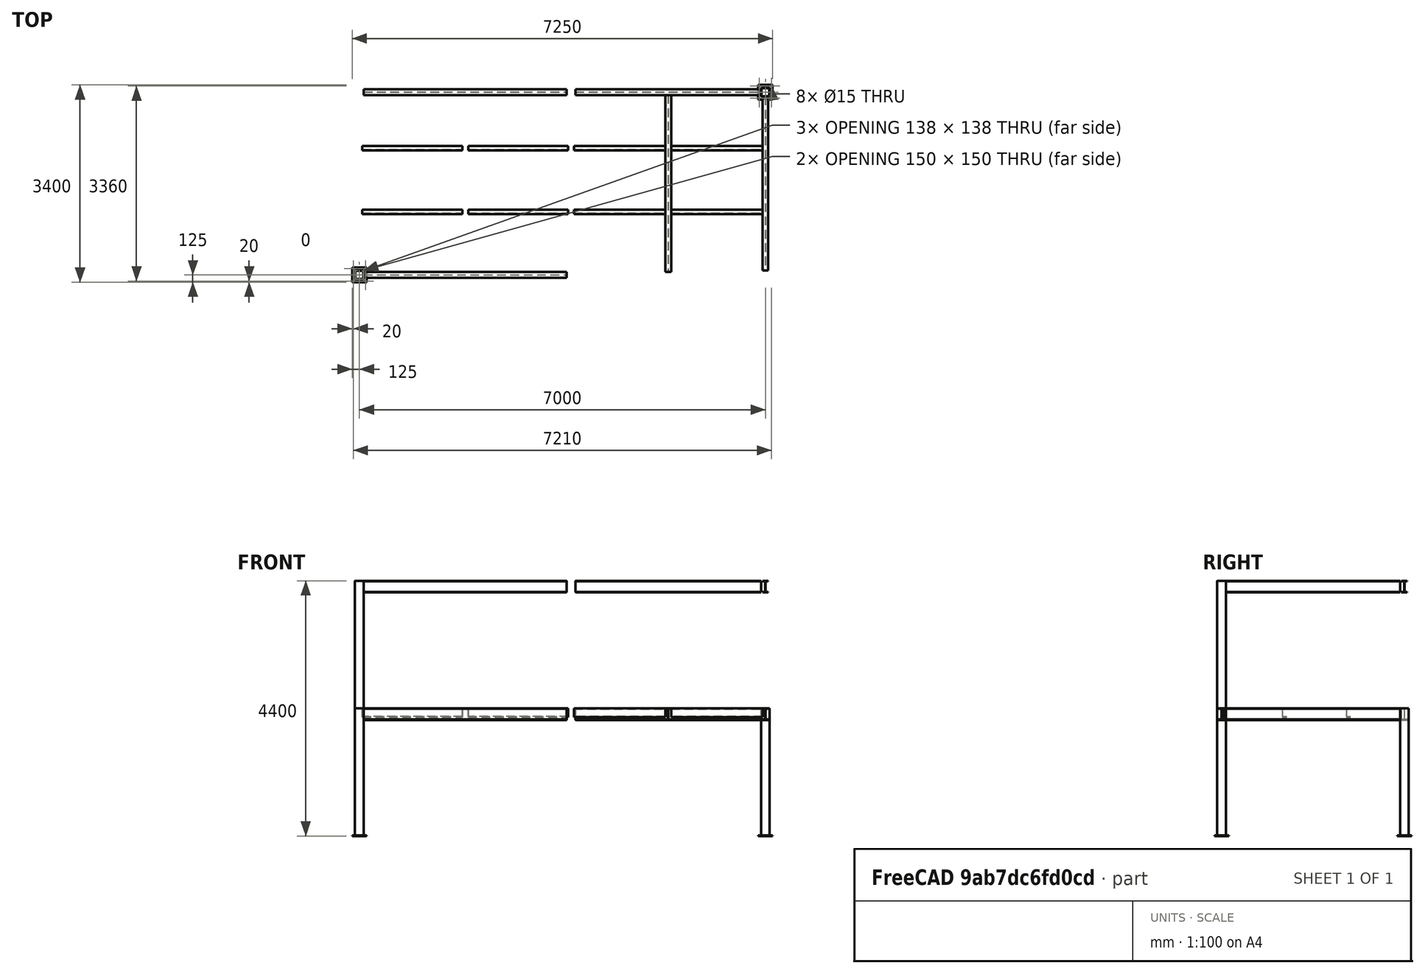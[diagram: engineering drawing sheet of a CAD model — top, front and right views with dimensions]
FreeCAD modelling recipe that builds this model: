
FCSTD DOCUMENT  (FreeCAD 0.21R30492 (Git))
Label: steelframe
License: All rights reserved
LicenseURL: http://en.wikipedia.org/wiki/All_rights_reserved
objects: App::FeaturePython×181, Part::FeaturePython×121, App::Link×12, Part::Extrusion×1, Part::MultiFuse×1
note: 122 computed .brp shape members not serialized (recipe doc carries the construction recipe); baked Part::Feature solids carry a one-line shape summary decoded from their .brp

FEATURE [Part::FeaturePython] BasePlate  # WARN: FeaturePython — macro-defined, semantics opaque (R4)
  B = 250
  D = 15
  H = 250
  b1 = 20
  h1 = 20
  sface = 0
FEATURE [Part::FeaturePython] SquarePipe_SS  # WARN: FeaturePython — macro-defined, semantics opaque (R4)
  L = 2200
  Solid = true
  size = 43
  standard = SS
FEATURE [Part::Extrusion] Extrude
  Base = -> BasePlate
  Dir = (0,0,1)
  DirMode = 2
  FaceMakerClass = Part::FaceMakerBullseye
  LengthFwd = 9
  LengthRev = 0
  Solid = true
  Symmetric = false
FEATURE [Part::MultiFuse] Fusion  label="Square-steel pipe"
  Placement = pos=(1.063e-12,6.983e-12,237) rot=(0,0,1;0rad)
  Shapes = -> [SquarePipe_SS,Extrude]
FEATURE [Part::FeaturePython] H200x100x5_5_8  label="H_thin"  # WARN: FeaturePython — macro-defined, semantics opaque (R4)
  L = 3000
  Placement = pos=(1.2035e-12,3075,2337) rot=(1,0,0;1.5708rad)
  Solid = true
  size = 5
  standard = SS_Thin
FEATURE [App::Link] Link  label="Square-steel pipe001"
  LinkPlacement = pos=(3650,2.14375e-11,237) rot=(0,0,1;0rad)
  LinkedObject = -> Fusion
  Placement = pos=(3650,2.14375e-11,237) rot=(0,0,1;0rad)
FEATURE [Part::FeaturePython] H200x100x5_5_009  label="H_thin001"  # WARN: FeaturePython — macro-defined, semantics opaque (R4)
  L = 3500
  Placement = pos=(75,-3.062e-12,2337) rot=(0.57735,0.57735,0.57735;2.0944rad)
  Solid = true
  size = 5
  standard = SS_Thin
  expr: L = 3500
FEATURE [App::Link] Link001  label="Square-steel pipe002"
  LinkPlacement = pos=(1.0657e-12,3150,237) rot=(0,0,1;0rad)
  LinkedObject = -> Fusion
  Placement = pos=(1.0657e-12,3150,237) rot=(0,0,1;0rad)
FEATURE [Part::FeaturePython] H200x100x5_5_010  label="H_thin002"  # WARN: FeaturePython — macro-defined, semantics opaque (R4)
  L = 3200
  Placement = pos=(3725,-8.67686e-11,2337) rot=(0.57735,0.57735,0.57735;2.0944rad)
  Solid = true
  size = 5
  standard = SS_Thin
FEATURE [App::Link] Link002  label="Square-steel pipe003"
  LinkPlacement = pos=(7000,-1.45687e-10,237) rot=(0,0,1;0rad)
  LinkedObject = -> Link
  Placement = pos=(7000,-1.45687e-10,237) rot=(0,0,1;0rad)
FEATURE [App::Link] Link003  label="H_thin003"
  LinkPlacement = pos=(75,3150,2337) rot=(0.57735,0.57735,0.57735;2.0944rad)
  LinkedObject = -> H200x100x5_5_009
  Placement = pos=(75,3150,2337) rot=(0.57735,0.57735,0.57735;2.0944rad)
FEATURE [App::Link] Link004  label="Square-steel pipe004"
  LinkPlacement = pos=(3650,3150,237) rot=(0,0,1;0rad)
  LinkedObject = -> Link
  Placement = pos=(3650,3150,237) rot=(0,0,1;0rad)
FEATURE [Part::FeaturePython] Clone  label="H_thin004"  # Draft clone (typed FeaturePython)
  AttacherType = Attacher::AttachEngine3D
  Fuse = false
  Objects = -> [H200x100x5_5_8]
  Placement = pos=(3650,3075,2337) rot=(1,0,0;1.5708rad)
  Scale = (1,1,1)
FEATURE [Part::FeaturePython] Clone001  label="H_thin005"  # Draft clone (typed FeaturePython)
  AttacherType = Attacher::AttachEngine3D
  Fuse = false
  Objects = -> [H200x100x5_5_010]
  Placement = pos=(3725,3150,2337) rot=(0.57735,0.57735,0.57735;2.0944rad)
  Scale = (1,1,1)
FEATURE [Part::FeaturePython] Clone002  label="Square-steel pipe005"  # Draft clone (typed FeaturePython)
  AttacherType = Attacher::AttachEngine3D
  Fuse = false
  Objects = -> [Link002]
  Placement = pos=(7000,3150,237) rot=(0,0,1;0rad)
  Scale = (1,1,1)
FEATURE [Part::FeaturePython] Clone003  label="H_thin006"  # Draft clone (typed FeaturePython)
  AttacherType = Attacher::AttachEngine3D
  Fuse = false
  Objects = -> [Clone]
  Placement = pos=(7000,3075,2337) rot=(1,0,0;1.5708rad)
  Scale = (1,1,1)
FEATURE [Part::FeaturePython] H200x100x5_5_011  label="H_thin007"  # WARN: FeaturePython — macro-defined, semantics opaque (R4)
  L = 3050
  Placement = pos=(1825,3100,2337) rot=(1,0,0;1.5708rad)
  Solid = true
  size = 5
  standard = SS_Thin
FEATURE [Part::FeaturePython] Clone004  label="H_thin008"  # Draft clone (typed FeaturePython)
  AttacherType = Attacher::AttachEngine3D
  Fuse = false
  Objects = -> [H200x100x5_5_011]
  Placement = pos=(5325,3100,2337) rot=(1,0,0;1.5708rad)
  Scale = (1,1,1)
FEATURE [Part::FeaturePython] C150x75x007  label="Channel001"  # WARN: FeaturePython — macro-defined, semantics opaque (R4)
  L = 1575
  Placement = pos=(3700,1086.25,2362) rot=(0.57735,0.57735,0.57735;2.0944rad)
  Solid = true
  size = 3
  standard = SS
FEATURE [Part::FeaturePython] C150x75x008  label="Channel002"  # WARN: FeaturePython — macro-defined, semantics opaque (R4)
  L = 1725
  Placement = pos=(50.0219,1086.25,2362) rot=(-0.57735,-0.57735,-0.57735;4.18879rad)
  Solid = true
  size = 3
  standard = SS
FEATURE [Part::FeaturePython] SquarePipe_SS001  label="SQ_Pipe"  # WARN: FeaturePython — macro-defined, semantics opaque (R4)
  L = 2200
  Placement = pos=(1.063e-12,2.583e-12,2437) rot=(0,0,1;2e-06rad)
  Solid = true
  size = 43
  standard = SS
FEATURE [App::Link] Link005  label="SQ_Pipe001"
  LinkPlacement = pos=(1.0843e-12,3150,2437) rot=(0,0,1;0rad)
  LinkedObject = -> SquarePipe_SS001
  Placement = pos=(1.0843e-12,3150,2437) rot=(0,0,1;0rad)
FEATURE [App::Link] Link006  label="SQ_Pipe002"
  LinkPlacement = pos=(3650,-1.01645e-10,2437) rot=(0,0,1;0rad)
  LinkedObject = -> SquarePipe_SS001
  Placement = pos=(3650,-1.01645e-10,2437) rot=(0,0,1;0rad)
FEATURE [App::Link] Link007  label="SQ_Pipe003"
  LinkPlacement = pos=(3650,3150,2437) rot=(0,0,1;0rad)
  LinkedObject = -> Link006
  Placement = pos=(3650,3150,2437) rot=(0,0,1;0rad)
FEATURE [App::Link] Link008  label="SQ_Pipe004"
  LinkPlacement = pos=(7000,6.50122e-10,2437) rot=(0,0,1;0rad)
  LinkedObject = -> Link007
  Placement = pos=(7000,6.50122e-10,2437) rot=(0,0,1;0rad)
FEATURE [App::Link] Link009  label="SQ_Pipe005"
  LinkPlacement = pos=(7000,3150,2437) rot=(0,0,1;0rad)
  LinkedObject = -> Link008
  Placement = pos=(7000,3150,2437) rot=(0,0,1;0rad)
FEATURE [App::Link] Link010  label="H_thin009"
  LinkPlacement = pos=(75,0.000150522,4537) rot=(0.577351,-0.57735,0.57735;4.18879rad)
  LinkedObject = -> H200x100x5_5_009
  Placement = pos=(75,0.000150522,4537) rot=(0.577351,-0.57735,0.57735;4.18879rad)
FEATURE [App::Link] Link011  label="H_thin010"
  LinkPlacement = pos=(-0.000150522,75,4537) rot=(-1,-1e-06,1e-06;1.5708rad)
  LinkedObject = -> H200x100x5_5_8
  Placement = pos=(-0.000150522,75,4537) rot=(-1,-1e-06,1e-06;1.5708rad)
FEATURE [Part::FeaturePython] Clone005  label="H_thin011"  # Draft clone (typed FeaturePython)
  AttacherType = Attacher::AttachEngine3D
  Fuse = false
  Objects = -> [H200x100x5_5_010]
  Placement = pos=(3725,-2.13896e-11,4537) rot=(0.57735,0.57735,0.57735;2.0944rad)
  Scale = (1,1,1)
FEATURE [Part::FeaturePython] Clone006  label="H_thin012"  # Draft clone (typed FeaturePython)
  AttacherType = Attacher::AttachEngine3D
  Fuse = false
  Objects = -> [Link011]
  Placement = pos=(3650,75,4537) rot=(-1,0,0;1.5708rad)
  Scale = (1,1,1)
FEATURE [Part::FeaturePython] Clone007  label="H_thin013"  # Draft clone (typed FeaturePython)
  AttacherType = Attacher::AttachEngine3D
  Fuse = false
  Objects = -> [Clone006]
  Placement = pos=(7000,75,4537) rot=(-1,0,0;1.5708rad)
  Scale = (1,1,1)
FEATURE [Part::FeaturePython] Clone008  label="H_thin014"  # Draft clone (typed FeaturePython)
  AttacherType = Attacher::AttachEngine3D
  Fuse = false
  Objects = -> [Link010]
  Placement = pos=(75,3150,4537) rot=(-0.57735,0.57735,-0.57735;2.0944rad)
  Scale = (1,1,1)
FEATURE [Part::FeaturePython] Clone009  label="H_thin015"  # Draft clone (typed FeaturePython)
  AttacherType = Attacher::AttachEngine3D
  Fuse = false
  Objects = -> [Clone005]
  Placement = pos=(3725,3150,4537) rot=(0.57735,0.57735,0.57735;2.0944rad)
  Scale = (1,1,1)
FEATURE [Part::FeaturePython] Array002  # Draft array (typed FeaturePython)
  Angle = 360
  ArrayType = 0
  Axis = (0,0,1)
  Base = -> C150x75x007
  Center = (0,0,0)
  Fuse = false
  IntervalAxis = (0,0,0)
  IntervalX = (1675,0,0)
  IntervalY = (0,1100,0)
  IntervalZ = (0,0,50)
  NumberCircles = 3
  NumberPolar = 5
  NumberX = 2
  NumberY = 2
  NumberZ = 1
  RadialDistance = 50
  Symmetry = 1
  TangentialDistance = 25
FEATURE [Part::FeaturePython] Array  # Draft array (typed FeaturePython)
  Angle = 360
  ArrayType = 0
  Axis = (0,0,1)
  Base = -> C150x75x008
  Center = (0,0,0)
  Fuse = false
  IntervalAxis = (0,0,0)
  IntervalX = (1826,0,0)
  IntervalY = (0,1100,0)
  IntervalZ = (0,0,50)
  NumberCircles = 3
  NumberPolar = 5
  NumberX = 2
  NumberY = 2
  NumberZ = 1
  RadialDistance = 50
  Symmetry = 1
  TangentialDistance = 25
FEATURE [Part::FeaturePython] Parts  # WARN: FeaturePython — macro-defined, semantics opaque (R4)
  Group = -> [Fusion,H200x100x5_5_8,Link,H200x100x5_5_009,Link001,H200x100x5_5_010,Link002,Link003,Link004,Clone,Clone001,Clone002,Clone003,H200x100x5_5_011,Clone004,C150x75x007,C150x75x008,SquarePipe_SS001,Link005,Link006,Link007,Link008,Link009,Link010,Link011,Clone005,Clone006,Clone007,Clone008,Clone009,Array002,Array]
  GroupMode = 0
FEATURE [Part::FeaturePython] Assembly  # WARN: FeaturePython — macro-defined, semantics opaque (R4)
  AutoRelax = true
  BuildShape = 0
  Freeze = false
  Group = -> [Constraints,Elements,Parts]
  Verbose = false
  _SolverType = 1
  _Version = 1
FEATURE [App::FeaturePython] Constraints  # WARN: FeaturePython — macro-defined, semantics opaque (R4)
  Group = -> [Constraint,Constraint001,Constraint002,Constraint003,Constraint004,Constraint005,Constraint006,Constraint007,Constraint008,Constraint009,Constraint010,Constraint011,Constraint012,Constraint013,Constraint014,Constraint015,Constraint016,Constraint017,Constraint018,Constraint019,Constraint020,Constraint021,Constraint022,Constraint023,Constraint024,Constraint025,Constraint026,Constraint027,+32 more]
  _Version = 1
FEATURE [App::FeaturePython] Elements  # WARN: FeaturePython — macro-defined, semantics opaque (R4)
  Group = -> [_Element,_Element001,_Element002,_Element003,_Element004,_Element005,_Element006,_Element007,_Element008,_Element009,_Element010,_Element011,_Element012,_Element013,_Element014,_Element015,_Element016,_Element017,_Element018,_Element019,_Element020,_Element021,_Element022,_Element023,_Element024,_Element025,_Element026,_Element027,_Element028,_Element029,_Element030,_Element031,_Element032,+65 more]
FEATURE [App::FeaturePython] Constraint  label="PlaneCoincident"  # WARN: FeaturePython — macro-defined, semantics opaque (R4)
  Angle = 0
  AnglePitch = 0
  AngleRoll = 0
  Cascade = false
  Disabled = false
  Group = -> [ElementLink,ElementLink001]
  LockAngle = false
  Multiply = false
  OffsetX = 0
  OffsetY = 0
  _ConstraintType = 35
  _Parent = -> Constraints
FEATURE [App::FeaturePython] ElementLink  label="_Element"  # link proxy (typed FeaturePython)
  LinkTransform = true
  LinkedObject = -> _Element
  _Parent = -> Constraint
FEATURE [Part::FeaturePython] _Element  # link proxy (typed FeaturePython)
  Detach = false
  LinkTransform = true
  LinkedObject = -> SquarePipe_SS001 [Face17]
  _Parent = -> Elements
FEATURE [App::FeaturePython] ElementLink001  label="_Element001"  # link proxy (typed FeaturePython)
  LinkTransform = true
  LinkedObject = -> _Element001
  _Parent = -> Constraint
FEATURE [Part::FeaturePython] _Element001  # link proxy (typed FeaturePython)
  Detach = false
  LinkTransform = true
  LinkedObject = -> Fusion [Face21]
  _Parent = -> Elements
FEATURE [Part::FeaturePython] _Element002  # link proxy (typed FeaturePython)
  Detach = false
  LinkTransform = true
  LinkedObject = -> H200x100x5_5_009 [Edge47]
  _Parent = -> Elements
FEATURE [Part::FeaturePython] _Element003  # link proxy (typed FeaturePython)
  Detach = false
  LinkTransform = true
  LinkedObject = -> Fusion [Edge59]
  _Parent = -> Elements
FEATURE [App::FeaturePython] Constraint001  label="Locked"  # WARN: FeaturePython — macro-defined, semantics opaque (R4)
  Disabled = false
  Group = -> [ElementLink002]
  _ConstraintType = 0
  _Parent = -> Constraints
FEATURE [App::FeaturePython] ElementLink002  label="_Element004"  # link proxy (typed FeaturePython)
  LinkTransform = true
  LinkedObject = -> _Element004
  _Parent = -> Constraint001
FEATURE [Part::FeaturePython] _Element004  # link proxy (typed FeaturePython)
  Detach = false
  LinkTransform = true
  LinkedObject = -> Fusion [Face16]
  _Parent = -> Elements
FEATURE [App::FeaturePython] Constraint002  label="MidPoint"  # WARN: FeaturePython — macro-defined, semantics opaque (R4)
  Disabled = false
  Group = -> [ElementLink003,ElementLink004]
  _ConstraintType = 20
  _Parent = -> Constraints
FEATURE [App::FeaturePython] ElementLink003  label="_Element002"  # link proxy (typed FeaturePython)
  LinkTransform = true
  LinkedObject = -> _Element002
  _Parent = -> Constraint002
FEATURE [App::FeaturePython] ElementLink004  label="_Element003"  # link proxy (typed FeaturePython)
  LinkTransform = true
  LinkedObject = -> _Element003
  _Parent = -> Constraint002
FEATURE [Part::FeaturePython] _Element005  # link proxy (typed FeaturePython)
  Detach = false
  LinkTransform = true
  LinkedObject = -> H200x100x5_5_009 [Vertex15]
  _Parent = -> Elements
FEATURE [App::FeaturePython] Constraint003  label="PlaneAlignment"  # WARN: FeaturePython — macro-defined, semantics opaque (R4)
  Angle = 0
  AnglePitch = 0
  AngleRoll = 0
  Cascade = false
  Disabled = false
  Group = -> [ElementLink005,ElementLink006]
  LockAngle = false
  _ConstraintType = 37
  _Parent = -> Constraints
FEATURE [App::FeaturePython] ElementLink005  label="_Element006"  # link proxy (typed FeaturePython)
  LinkTransform = true
  LinkedObject = -> _Element006
  _Parent = -> Constraint003
FEATURE [Part::FeaturePython] _Element006  # link proxy (typed FeaturePython)
  Detach = false
  LinkTransform = true
  LinkedObject = -> H200x100x5_5_009 [Face16]
  _Parent = -> Elements
FEATURE [App::FeaturePython] ElementLink006  label="_Element001"  # link proxy (typed FeaturePython)
  LinkTransform = true
  LinkedObject = -> _Element001
  _Parent = -> Constraint003
FEATURE [App::FeaturePython] Constraint004  label="SameOrientation"  # WARN: FeaturePython — macro-defined, semantics opaque (R4)
  Disabled = false
  Group = -> [ElementLink007,ElementLink008]
  _ConstraintType = 2
  _Parent = -> Constraints
FEATURE [App::FeaturePython] ElementLink007  label="_Element006"  # link proxy (typed FeaturePython)
  LinkTransform = true
  LinkedObject = -> _Element006
  _Parent = -> Constraint004
FEATURE [App::FeaturePython] ElementLink008  label="_Element001"  # link proxy (typed FeaturePython)
  LinkTransform = true
  LinkedObject = -> _Element001
  _Parent = -> Constraint004
FEATURE [App::FeaturePython] Constraint005  label="MidPoint001"  # WARN: FeaturePython — macro-defined, semantics opaque (R4)
  Disabled = false
  Group = -> [ElementLink009,ElementLink010]
  _ConstraintType = 20
  _Parent = -> Constraints
FEATURE [App::FeaturePython] ElementLink009  label="_Element007"  # link proxy (typed FeaturePython)
  LinkTransform = true
  LinkedObject = -> _Element007
  _Parent = -> Constraint005
FEATURE [Part::FeaturePython] _Element007  # link proxy (typed FeaturePython)
  Detach = false
  LinkTransform = true
  LinkedObject = -> H200x100x5_5_009 [Edge48]
  _Parent = -> Elements
FEATURE [App::FeaturePython] ElementLink010  label="_Element008"  # link proxy (typed FeaturePython)
  LinkTransform = true
  LinkedObject = -> _Element008
  _Parent = -> Constraint005
FEATURE [Part::FeaturePython] _Element008  # link proxy (typed FeaturePython)
  Detach = false
  LinkTransform = true
  LinkedObject = -> Link [Edge50]
  _Parent = -> Elements
FEATURE [App::FeaturePython] Constraint006  label="SameOrientation001"  # WARN: FeaturePython — macro-defined, semantics opaque (R4)
  Disabled = false
  Group = -> [ElementLink011,ElementLink012]
  _ConstraintType = 2
  _Parent = -> Constraints
FEATURE [App::FeaturePython] ElementLink011  label="_Element006"  # link proxy (typed FeaturePython)
  LinkTransform = true
  LinkedObject = -> _Element006
  _Parent = -> Constraint006
FEATURE [App::FeaturePython] ElementLink012  label="_Element009"  # link proxy (typed FeaturePython)
  LinkTransform = true
  LinkedObject = -> _Element009
  _Parent = -> Constraint006
FEATURE [Part::FeaturePython] _Element009  # link proxy (typed FeaturePython)
  Detach = false
  LinkTransform = true
  LinkedObject = -> Link [Face21]
  _Parent = -> Elements
FEATURE [App::FeaturePython] Constraint007  label="MidPoint002"  # WARN: FeaturePython — macro-defined, semantics opaque (R4)
  Disabled = false
  Group = -> [ElementLink013,ElementLink014]
  _ConstraintType = 20
  _Parent = -> Constraints
FEATURE [App::FeaturePython] ElementLink013  label="_Element010"  # link proxy (typed FeaturePython)
  LinkTransform = true
  LinkedObject = -> _Element010
  _Parent = -> Constraint007
FEATURE [Part::FeaturePython] _Element010  # link proxy (typed FeaturePython)
  Detach = false
  LinkTransform = true
  LinkedObject = -> Link006 [Edge18]
  _Parent = -> Elements
FEATURE [App::FeaturePython] ElementLink014  label="_Element011"  # link proxy (typed FeaturePython)
  LinkTransform = true
  LinkedObject = -> _Element011
  _Parent = -> Constraint007
FEATURE [Part::FeaturePython] _Element011  # link proxy (typed FeaturePython)
  Detach = false
  LinkTransform = true
  LinkedObject = -> Link [Edge55]
  _Parent = -> Elements
FEATURE [App::FeaturePython] Constraint008  label="SameOrientation002"  # WARN: FeaturePython — macro-defined, semantics opaque (R4)
  Disabled = false
  Group = -> [ElementLink015,ElementLink016]
  _ConstraintType = 2
  _Parent = -> Constraints
FEATURE [App::FeaturePython] ElementLink015  label="_Element012"  # link proxy (typed FeaturePython)
  LinkTransform = true
  LinkedObject = -> _Element012
  _Parent = -> Constraint008
FEATURE [Part::FeaturePython] _Element012  # link proxy (typed FeaturePython)
  Detach = false
  LinkTransform = true
  LinkedObject = -> Link006 [Face6]
  _Parent = -> Elements
FEATURE [App::FeaturePython] ElementLink016  label="_Element013"  # link proxy (typed FeaturePython)
  LinkTransform = true
  LinkedObject = -> _Element013
  _Parent = -> Constraint008
FEATURE [Part::FeaturePython] _Element013  # link proxy (typed FeaturePython)
  Detach = false
  LinkTransform = true
  LinkedObject = -> Link [Face14]
  _Parent = -> Elements
FEATURE [App::FeaturePython] Constraint009  label="MidPoint003"  # WARN: FeaturePython — macro-defined, semantics opaque (R4)
  Disabled = false
  Group = -> [ElementLink017,ElementLink018]
  _ConstraintType = 20
  _Parent = -> Constraints
FEATURE [App::FeaturePython] ElementLink017  label="_Element014"  # link proxy (typed FeaturePython)
  LinkTransform = true
  LinkedObject = -> _Element014
  _Parent = -> Constraint009
FEATURE [Part::FeaturePython] _Element014  # link proxy (typed FeaturePython)
  Detach = false
  LinkTransform = true
  LinkedObject = -> H200x100x5_5_010 [Edge47]
  _Parent = -> Elements
FEATURE [App::FeaturePython] ElementLink018  label="_Element015"  # link proxy (typed FeaturePython)
  LinkTransform = true
  LinkedObject = -> _Element015
  _Parent = -> Constraint009
FEATURE [Part::FeaturePython] _Element015  # link proxy (typed FeaturePython)
  Detach = false
  LinkTransform = true
  LinkedObject = -> Link006 [Edge12]
  _Parent = -> Elements
FEATURE [App::FeaturePython] Constraint010  label="SameOrientation003"  # WARN: FeaturePython — macro-defined, semantics opaque (R4)
  Disabled = false
  Group = -> [ElementLink019,ElementLink020]
  _ConstraintType = 2
  _Parent = -> Constraints
FEATURE [App::FeaturePython] ElementLink019  label="_Element016"  # link proxy (typed FeaturePython)
  LinkTransform = true
  LinkedObject = -> _Element016
  _Parent = -> Constraint010
FEATURE [Part::FeaturePython] _Element016  # link proxy (typed FeaturePython)
  Detach = false
  LinkTransform = true
  LinkedObject = -> H200x100x5_5_010 [Face16]
  _Parent = -> Elements
FEATURE [App::FeaturePython] ElementLink020  label="_Element009"  # link proxy (typed FeaturePython)
  LinkTransform = true
  LinkedObject = -> _Element009
  _Parent = -> Constraint010
FEATURE [App::FeaturePython] Constraint011  label="MidPoint004"  # WARN: FeaturePython — macro-defined, semantics opaque (R4)
  Disabled = false
  Group = -> [ElementLink021,ElementLink022]
  _ConstraintType = 20
  _Parent = -> Constraints
FEATURE [App::FeaturePython] ElementLink021  label="_Element017"  # link proxy (typed FeaturePython)
  LinkTransform = true
  LinkedObject = -> _Element017
  _Parent = -> Constraint011
FEATURE [Part::FeaturePython] _Element017  # link proxy (typed FeaturePython)
  Detach = false
  LinkTransform = true
  LinkedObject = -> Link002 [Edge50]
  _Parent = -> Elements
FEATURE [App::FeaturePython] ElementLink022  label="_Element018"  # link proxy (typed FeaturePython)
  LinkTransform = true
  LinkedObject = -> _Element018
  _Parent = -> Constraint011
FEATURE [Part::FeaturePython] _Element018  # link proxy (typed FeaturePython)
  Detach = false
  LinkTransform = true
  LinkedObject = -> H200x100x5_5_010 [Edge48]
  _Parent = -> Elements
FEATURE [App::FeaturePython] Constraint012  label="SameOrientation004"  # WARN: FeaturePython — macro-defined, semantics opaque (R4)
  Disabled = false
  Group = -> [ElementLink023,ElementLink024]
  _ConstraintType = 2
  _Parent = -> Constraints
FEATURE [App::FeaturePython] ElementLink023  label="_Element016"  # link proxy (typed FeaturePython)
  LinkTransform = true
  LinkedObject = -> _Element016
  _Parent = -> Constraint012
FEATURE [App::FeaturePython] ElementLink024  label="_Element019"  # link proxy (typed FeaturePython)
  LinkTransform = true
  LinkedObject = -> _Element019
  _Parent = -> Constraint012
FEATURE [Part::FeaturePython] _Element019  # link proxy (typed FeaturePython)
  Detach = false
  LinkTransform = true
  LinkedObject = -> Link002 [Face21]
  _Parent = -> Elements
FEATURE [App::FeaturePython] Constraint013  label="MidPoint005"  # WARN: FeaturePython — macro-defined, semantics opaque (R4)
  Disabled = false
  Group = -> [ElementLink025,ElementLink026]
  _ConstraintType = 20
  _Parent = -> Constraints
FEATURE [App::FeaturePython] ElementLink025  label="_Element020"  # link proxy (typed FeaturePython)
  LinkTransform = true
  LinkedObject = -> _Element020
  _Parent = -> Constraint013
FEATURE [Part::FeaturePython] _Element020  # link proxy (typed FeaturePython)
  Detach = false
  LinkTransform = true
  LinkedObject = -> Link008 [Edge18]
  _Parent = -> Elements
FEATURE [App::FeaturePython] ElementLink026  label="_Element021"  # link proxy (typed FeaturePython)
  LinkTransform = true
  LinkedObject = -> _Element021
  _Parent = -> Constraint013
FEATURE [Part::FeaturePython] _Element021  # link proxy (typed FeaturePython)
  Detach = false
  LinkTransform = true
  LinkedObject = -> Link002 [Edge55]
  _Parent = -> Elements
FEATURE [App::FeaturePython] Constraint014  label="SameOrientation005"  # WARN: FeaturePython — macro-defined, semantics opaque (R4)
  Disabled = false
  Group = -> [ElementLink027,ElementLink028]
  _ConstraintType = 2
  _Parent = -> Constraints
FEATURE [App::FeaturePython] ElementLink027  label="_Element022"  # link proxy (typed FeaturePython)
  LinkTransform = true
  LinkedObject = -> _Element022
  _Parent = -> Constraint014
FEATURE [Part::FeaturePython] _Element022  # link proxy (typed FeaturePython)
  Detach = false
  LinkTransform = true
  LinkedObject = -> Link008 [Face6]
  _Parent = -> Elements
FEATURE [App::FeaturePython] ElementLink028  label="_Element023"  # link proxy (typed FeaturePython)
  LinkTransform = true
  LinkedObject = -> _Element023
  _Parent = -> Constraint014
FEATURE [Part::FeaturePython] _Element023  # link proxy (typed FeaturePython)
  Detach = false
  LinkTransform = true
  LinkedObject = -> Link002 [Face14]
  _Parent = -> Elements
FEATURE [App::FeaturePython] Constraint015  label="MidPoint006"  # WARN: FeaturePython — macro-defined, semantics opaque (R4)
  Disabled = false
  Group = -> [ElementLink029,ElementLink030]
  _ConstraintType = 20
  _Parent = -> Constraints
FEATURE [App::FeaturePython] ElementLink029  label="_Element024"  # link proxy (typed FeaturePython)
  LinkTransform = true
  LinkedObject = -> _Element024
  _Parent = -> Constraint015
FEATURE [Part::FeaturePython] _Element024  # link proxy (typed FeaturePython)
  Detach = false
  LinkTransform = true
  LinkedObject = -> H200x100x5_5_8 [Edge48]
  _Parent = -> Elements
FEATURE [App::FeaturePython] ElementLink030  label="_Element025"  # link proxy (typed FeaturePython)
  LinkTransform = true
  LinkedObject = -> _Element025
  _Parent = -> Constraint015
FEATURE [Part::FeaturePython] _Element025  # link proxy (typed FeaturePython)
  Detach = false
  LinkTransform = true
  LinkedObject = -> Fusion [Edge63]
  _Parent = -> Elements
FEATURE [App::FeaturePython] Constraint016  label="SameOrientation006"  # WARN: FeaturePython — macro-defined, semantics opaque (R4)
  Disabled = false
  Group = -> [ElementLink031,ElementLink032]
  _ConstraintType = 2
  _Parent = -> Constraints
FEATURE [App::FeaturePython] ElementLink031  label="_Element026"  # link proxy (typed FeaturePython)
  LinkTransform = true
  LinkedObject = -> _Element026
  _Parent = -> Constraint016
FEATURE [Part::FeaturePython] _Element026  # link proxy (typed FeaturePython)
  Detach = false
  LinkTransform = true
  LinkedObject = -> H200x100x5_5_8 [Face16]
  _Parent = -> Elements
FEATURE [App::FeaturePython] ElementLink032  label="_Element001"  # link proxy (typed FeaturePython)
  LinkTransform = true
  LinkedObject = -> _Element001
  _Parent = -> Constraint016
FEATURE [App::FeaturePython] Constraint017  label="MidPoint007"  # WARN: FeaturePython — macro-defined, semantics opaque (R4)
  Disabled = false
  Group = -> [ElementLink033,ElementLink034]
  _ConstraintType = 20
  _Parent = -> Constraints
FEATURE [App::FeaturePython] ElementLink033  label="_Element027"  # link proxy (typed FeaturePython)
  LinkTransform = true
  LinkedObject = -> _Element027
  _Parent = -> Constraint017
FEATURE [Part::FeaturePython] _Element027  # link proxy (typed FeaturePython)
  Detach = false
  LinkTransform = true
  LinkedObject = -> Clone [Edge48]
  _Parent = -> Elements
FEATURE [App::FeaturePython] ElementLink034  label="_Element028"  # link proxy (typed FeaturePython)
  LinkTransform = true
  LinkedObject = -> _Element028
  _Parent = -> Constraint017
FEATURE [Part::FeaturePython] _Element028  # link proxy (typed FeaturePython)
  Detach = false
  LinkTransform = true
  LinkedObject = -> Link [Edge63]
  _Parent = -> Elements
FEATURE [App::FeaturePython] Constraint018  label="SameOrientation007"  # WARN: FeaturePython — macro-defined, semantics opaque (R4)
  Disabled = false
  Group = -> [ElementLink035,ElementLink036]
  _ConstraintType = 2
  _Parent = -> Constraints
FEATURE [App::FeaturePython] ElementLink035  label="_Element029"  # link proxy (typed FeaturePython)
  LinkTransform = true
  LinkedObject = -> _Element029
  _Parent = -> Constraint018
FEATURE [Part::FeaturePython] _Element029  # link proxy (typed FeaturePython)
  Detach = false
  LinkTransform = true
  LinkedObject = -> Clone [Face16]
  _Parent = -> Elements
FEATURE [App::FeaturePython] ElementLink036  label="_Element009"  # link proxy (typed FeaturePython)
  LinkTransform = true
  LinkedObject = -> _Element009
  _Parent = -> Constraint018
FEATURE [App::FeaturePython] Constraint019  label="MidPoint008"  # WARN: FeaturePython — macro-defined, semantics opaque (R4)
  Disabled = false
  Group = -> [ElementLink037,ElementLink038]
  _ConstraintType = 20
  _Parent = -> Constraints
FEATURE [App::FeaturePython] ElementLink037  label="_Element030"  # link proxy (typed FeaturePython)
  LinkTransform = true
  LinkedObject = -> _Element030
  _Parent = -> Constraint019
FEATURE [Part::FeaturePython] _Element030  # link proxy (typed FeaturePython)
  Detach = false
  LinkTransform = true
  LinkedObject = -> Clone003 [Edge48]
  _Parent = -> Elements
FEATURE [App::FeaturePython] ElementLink038  label="_Element031"  # link proxy (typed FeaturePython)
  LinkTransform = true
  LinkedObject = -> _Element031
  _Parent = -> Constraint019
FEATURE [Part::FeaturePython] _Element031  # link proxy (typed FeaturePython)
  Detach = false
  LinkTransform = true
  LinkedObject = -> Link002 [Edge63]
  _Parent = -> Elements
FEATURE [App::FeaturePython] Constraint020  label="SameOrientation008"  # WARN: FeaturePython — macro-defined, semantics opaque (R4)
  Disabled = false
  Group = -> [ElementLink039,ElementLink040]
  _ConstraintType = 2
  _Parent = -> Constraints
FEATURE [App::FeaturePython] ElementLink039  label="_Element032"  # link proxy (typed FeaturePython)
  LinkTransform = true
  LinkedObject = -> _Element032
  _Parent = -> Constraint020
FEATURE [Part::FeaturePython] _Element032  # link proxy (typed FeaturePython)
  Detach = false
  LinkTransform = true
  LinkedObject = -> Clone003 [Face16]
  _Parent = -> Elements
FEATURE [App::FeaturePython] ElementLink040  label="_Element019"  # link proxy (typed FeaturePython)
  LinkTransform = true
  LinkedObject = -> _Element019
  _Parent = -> Constraint020
FEATURE [App::FeaturePython] Constraint021  label="MidPoint009"  # WARN: FeaturePython — macro-defined, semantics opaque (R4)
  Disabled = false
  Group = -> [ElementLink041,ElementLink042]
  _ConstraintType = 20
  _Parent = -> Constraints
FEATURE [App::FeaturePython] ElementLink041  label="_Element033"  # link proxy (typed FeaturePython)
  LinkTransform = true
  LinkedObject = -> _Element033
  _Parent = -> Constraint021
FEATURE [Part::FeaturePython] _Element033  # link proxy (typed FeaturePython)
  Detach = false
  LinkTransform = true
  LinkedObject = -> Link001 [Edge55]
  _Parent = -> Elements
FEATURE [App::FeaturePython] ElementLink042  label="_Element034"  # link proxy (typed FeaturePython)
  LinkTransform = true
  LinkedObject = -> _Element034
  _Parent = -> Constraint021
FEATURE [Part::FeaturePython] _Element034  # link proxy (typed FeaturePython)
  Detach = false
  LinkTransform = true
  LinkedObject = -> H200x100x5_5_8 [Edge47]
  _Parent = -> Elements
FEATURE [App::FeaturePython] Constraint022  label="SameOrientation009"  # WARN: FeaturePython — macro-defined, semantics opaque (R4)
  Disabled = false
  Group = -> [ElementLink043,ElementLink044]
  _ConstraintType = 2
  _Parent = -> Constraints
FEATURE [App::FeaturePython] ElementLink043  label="_Element026"  # link proxy (typed FeaturePython)
  LinkTransform = true
  LinkedObject = -> _Element026
  _Parent = -> Constraint022
FEATURE [App::FeaturePython] ElementLink044  label="_Element035"  # link proxy (typed FeaturePython)
  LinkTransform = true
  LinkedObject = -> _Element035
  _Parent = -> Constraint022
FEATURE [Part::FeaturePython] _Element035  # link proxy (typed FeaturePython)
  Detach = false
  LinkTransform = true
  LinkedObject = -> Link001 [Face21]
  _Parent = -> Elements
FEATURE [App::FeaturePython] Constraint023  label="MidPoint010"  # WARN: FeaturePython — macro-defined, semantics opaque (R4)
  Disabled = false
  Group = -> [ElementLink045,ElementLink046]
  _ConstraintType = 20
  _Parent = -> Constraints
FEATURE [App::FeaturePython] ElementLink045  label="_Element036"  # link proxy (typed FeaturePython)
  LinkTransform = true
  LinkedObject = -> _Element036
  _Parent = -> Constraint023
FEATURE [Part::FeaturePython] _Element036  # link proxy (typed FeaturePython)
  Detach = false
  LinkTransform = true
  LinkedObject = -> Link005 [Edge12]
  _Parent = -> Elements
FEATURE [App::FeaturePython] ElementLink046  label="_Element037"  # link proxy (typed FeaturePython)
  LinkTransform = true
  LinkedObject = -> _Element037
  _Parent = -> Constraint023
FEATURE [Part::FeaturePython] _Element037  # link proxy (typed FeaturePython)
  Detach = false
  LinkTransform = true
  LinkedObject = -> Link001 [Edge59]
  _Parent = -> Elements
FEATURE [App::FeaturePython] Constraint024  label="SameOrientation010"  # WARN: FeaturePython — macro-defined, semantics opaque (R4)
  Disabled = false
  Group = -> [ElementLink047,ElementLink048]
  _ConstraintType = 2
  _Parent = -> Constraints
FEATURE [App::FeaturePython] ElementLink047  label="_Element038"  # link proxy (typed FeaturePython)
  LinkTransform = true
  LinkedObject = -> _Element038
  _Parent = -> Constraint024
FEATURE [Part::FeaturePython] _Element038  # link proxy (typed FeaturePython)
  Detach = false
  LinkTransform = true
  LinkedObject = -> Link001 [Face16]
  _Parent = -> Elements
FEATURE [App::FeaturePython] ElementLink048  label="_Element039"  # link proxy (typed FeaturePython)
  LinkTransform = true
  LinkedObject = -> _Element039
  _Parent = -> Constraint024
FEATURE [Part::FeaturePython] _Element039  # link proxy (typed FeaturePython)
  Detach = false
  LinkTransform = true
  LinkedObject = -> Link005 [Face4]
  _Parent = -> Elements
FEATURE [App::FeaturePython] Constraint025  label="MidPoint011"  # WARN: FeaturePython — macro-defined, semantics opaque (R4)
  Disabled = false
  Group = -> [ElementLink049,ElementLink050]
  _ConstraintType = 20
  _Parent = -> Constraints
FEATURE [App::FeaturePython] ElementLink049  label="_Element040"  # link proxy (typed FeaturePython)
  LinkTransform = true
  LinkedObject = -> _Element040
  _Parent = -> Constraint025
FEATURE [Part::FeaturePython] _Element040  # link proxy (typed FeaturePython)
  Detach = false
  LinkTransform = true
  LinkedObject = -> Clone [Edge47]
  _Parent = -> Elements
FEATURE [App::FeaturePython] ElementLink050  label="_Element041"  # link proxy (typed FeaturePython)
  LinkTransform = true
  LinkedObject = -> _Element041
  _Parent = -> Constraint025
FEATURE [Part::FeaturePython] _Element041  # link proxy (typed FeaturePython)
  Detach = false
  LinkTransform = true
  LinkedObject = -> Link004 [Edge55]
  _Parent = -> Elements
FEATURE [App::FeaturePython] Constraint026  label="SameOrientation011"  # WARN: FeaturePython — macro-defined, semantics opaque (R4)
  Disabled = false
  Group = -> [ElementLink051,ElementLink052]
  _ConstraintType = 2
  _Parent = -> Constraints
FEATURE [App::FeaturePython] ElementLink051  label="_Element029"  # link proxy (typed FeaturePython)
  LinkTransform = true
  LinkedObject = -> _Element029
  _Parent = -> Constraint026
FEATURE [App::FeaturePython] ElementLink052  label="_Element042"  # link proxy (typed FeaturePython)
  LinkTransform = true
  LinkedObject = -> _Element042
  _Parent = -> Constraint026
FEATURE [Part::FeaturePython] _Element042  # link proxy (typed FeaturePython)
  Detach = false
  LinkTransform = true
  LinkedObject = -> Link004 [Face21]
  _Parent = -> Elements
FEATURE [App::FeaturePython] Constraint027  label="MidPoint012"  # WARN: FeaturePython — macro-defined, semantics opaque (R4)
  Disabled = false
  Group = -> [ElementLink053,ElementLink054]
  _ConstraintType = 20
  _Parent = -> Constraints
FEATURE [App::FeaturePython] ElementLink053  label="_Element043"  # link proxy (typed FeaturePython)
  LinkTransform = true
  LinkedObject = -> _Element043
  _Parent = -> Constraint027
FEATURE [Part::FeaturePython] _Element043  # link proxy (typed FeaturePython)
  Detach = false
  LinkTransform = true
  LinkedObject = -> Link007 [Edge12]
  _Parent = -> Elements
FEATURE [App::FeaturePython] ElementLink054  label="_Element044"  # link proxy (typed FeaturePython)
  LinkTransform = true
  LinkedObject = -> _Element044
  _Parent = -> Constraint027
FEATURE [Part::FeaturePython] _Element044  # link proxy (typed FeaturePython)
  Detach = false
  LinkTransform = true
  LinkedObject = -> Link004 [Edge59]
  _Parent = -> Elements
FEATURE [App::FeaturePython] Constraint028  label="SameOrientation012"  # WARN: FeaturePython — macro-defined, semantics opaque (R4)
  Disabled = false
  Group = -> [ElementLink055,ElementLink056]
  _ConstraintType = 2
  _Parent = -> Constraints
FEATURE [App::FeaturePython] ElementLink055  label="_Element045"  # link proxy (typed FeaturePython)
  LinkTransform = true
  LinkedObject = -> _Element045
  _Parent = -> Constraint028
FEATURE [Part::FeaturePython] _Element045  # link proxy (typed FeaturePython)
  Detach = false
  LinkTransform = true
  LinkedObject = -> Link007 [Face4]
  _Parent = -> Elements
FEATURE [App::FeaturePython] ElementLink056  label="_Element046"  # link proxy (typed FeaturePython)
  LinkTransform = true
  LinkedObject = -> _Element046
  _Parent = -> Constraint028
FEATURE [Part::FeaturePython] _Element046  # link proxy (typed FeaturePython)
  Detach = false
  LinkTransform = true
  LinkedObject = -> Link004 [Face16]
  _Parent = -> Elements
FEATURE [App::FeaturePython] Constraint029  label="MidPoint013"  # WARN: FeaturePython — macro-defined, semantics opaque (R4)
  Disabled = false
  Group = -> [ElementLink057,ElementLink058]
  _ConstraintType = 20
  _Parent = -> Constraints
FEATURE [App::FeaturePython] ElementLink057  label="_Element047"  # link proxy (typed FeaturePython)
  LinkTransform = true
  LinkedObject = -> _Element047
  _Parent = -> Constraint029
FEATURE [Part::FeaturePython] _Element047  # link proxy (typed FeaturePython)
  Detach = false
  LinkTransform = true
  LinkedObject = -> Clone001 [Edge47]
  _Parent = -> Elements
FEATURE [App::FeaturePython] ElementLink058  label="_Element044"  # link proxy (typed FeaturePython)
  LinkTransform = true
  LinkedObject = -> _Element044
  _Parent = -> Constraint029
FEATURE [App::FeaturePython] Constraint030  label="SameOrientation013"  # WARN: FeaturePython — macro-defined, semantics opaque (R4)
  Disabled = false
  Group = -> [ElementLink059,ElementLink060]
  _ConstraintType = 2
  _Parent = -> Constraints
FEATURE [App::FeaturePython] ElementLink059  label="_Element048"  # link proxy (typed FeaturePython)
  LinkTransform = true
  LinkedObject = -> _Element048
  _Parent = -> Constraint030
FEATURE [Part::FeaturePython] _Element048  # link proxy (typed FeaturePython)
  Detach = false
  LinkTransform = true
  LinkedObject = -> Clone001 [Face16]
  _Parent = -> Elements
FEATURE [App::FeaturePython] ElementLink060  label="_Element042"  # link proxy (typed FeaturePython)
  LinkTransform = true
  LinkedObject = -> _Element042
  _Parent = -> Constraint030
FEATURE [App::FeaturePython] Constraint031  label="MidPoint014"  # WARN: FeaturePython — macro-defined, semantics opaque (R4)
  Disabled = false
  Group = -> [ElementLink061,ElementLink062]
  _ConstraintType = 20
  _Parent = -> Constraints
FEATURE [App::FeaturePython] ElementLink061  label="_Element049"  # link proxy (typed FeaturePython)
  LinkTransform = true
  LinkedObject = -> _Element049
  _Parent = -> Constraint031
FEATURE [Part::FeaturePython] _Element049  # link proxy (typed FeaturePython)
  Detach = false
  LinkTransform = true
  LinkedObject = -> Clone002 [Edge55]
  _Parent = -> Elements
FEATURE [App::FeaturePython] ElementLink062  label="_Element050"  # link proxy (typed FeaturePython)
  LinkTransform = true
  LinkedObject = -> _Element050
  _Parent = -> Constraint031
FEATURE [Part::FeaturePython] _Element050  # link proxy (typed FeaturePython)
  Detach = false
  LinkTransform = true
  LinkedObject = -> Clone003 [Edge47]
  _Parent = -> Elements
FEATURE [App::FeaturePython] Constraint032  label="SameOrientation014"  # WARN: FeaturePython — macro-defined, semantics opaque (R4)
  Disabled = false
  Group = -> [ElementLink063,ElementLink064]
  _ConstraintType = 2
  _Parent = -> Constraints
FEATURE [App::FeaturePython] ElementLink063  label="_Element032"  # link proxy (typed FeaturePython)
  LinkTransform = true
  LinkedObject = -> _Element032
  _Parent = -> Constraint032
FEATURE [App::FeaturePython] ElementLink064  label="_Element051"  # link proxy (typed FeaturePython)
  LinkTransform = true
  LinkedObject = -> _Element051
  _Parent = -> Constraint032
FEATURE [Part::FeaturePython] _Element051  # link proxy (typed FeaturePython)
  Detach = false
  LinkTransform = true
  LinkedObject = -> Clone002 [Face21]
  _Parent = -> Elements
FEATURE [App::FeaturePython] Constraint033  label="MidPoint015"  # WARN: FeaturePython — macro-defined, semantics opaque (R4)
  Disabled = false
  Group = -> [ElementLink065,ElementLink066]
  _ConstraintType = 20
  _Parent = -> Constraints
FEATURE [App::FeaturePython] ElementLink065  label="_Element052"  # link proxy (typed FeaturePython)
  LinkTransform = true
  LinkedObject = -> _Element052
  _Parent = -> Constraint033
FEATURE [Part::FeaturePython] _Element052  # link proxy (typed FeaturePython)
  Detach = false
  LinkTransform = true
  LinkedObject = -> Link009 [Edge12]
  _Parent = -> Elements
FEATURE [App::FeaturePython] ElementLink066  label="_Element053"  # link proxy (typed FeaturePython)
  LinkTransform = true
  LinkedObject = -> _Element053
  _Parent = -> Constraint033
FEATURE [Part::FeaturePython] _Element053  # link proxy (typed FeaturePython)
  Detach = false
  LinkTransform = true
  LinkedObject = -> Clone002 [Edge59]
  _Parent = -> Elements
FEATURE [App::FeaturePython] Constraint034  label="SameOrientation015"  # WARN: FeaturePython — macro-defined, semantics opaque (R4)
  Disabled = false
  Group = -> [ElementLink067,ElementLink068]
  _ConstraintType = 2
  _Parent = -> Constraints
FEATURE [App::FeaturePython] ElementLink067  label="_Element054"  # link proxy (typed FeaturePython)
  LinkTransform = true
  LinkedObject = -> _Element054
  _Parent = -> Constraint034
FEATURE [Part::FeaturePython] _Element054  # link proxy (typed FeaturePython)
  Detach = false
  LinkTransform = true
  LinkedObject = -> Clone002 [Face16]
  _Parent = -> Elements
FEATURE [App::FeaturePython] ElementLink068  label="_Element055"  # link proxy (typed FeaturePython)
  LinkTransform = true
  LinkedObject = -> _Element055
  _Parent = -> Constraint034
FEATURE [Part::FeaturePython] _Element055  # link proxy (typed FeaturePython)
  Detach = false
  LinkTransform = true
  LinkedObject = -> Link009 [Face4]
  _Parent = -> Elements
FEATURE [App::FeaturePython] Constraint035  label="MidPoint016"  # WARN: FeaturePython — macro-defined, semantics opaque (R4)
  Disabled = false
  Group = -> [ElementLink069,ElementLink070]
  _ConstraintType = 20
  _Parent = -> Constraints
FEATURE [App::FeaturePython] ElementLink069  label="_Element056"  # link proxy (typed FeaturePython)
  LinkTransform = true
  LinkedObject = -> _Element056
  _Parent = -> Constraint035
FEATURE [Part::FeaturePython] _Element056  # link proxy (typed FeaturePython)
  Detach = false
  LinkTransform = true
  LinkedObject = -> Link010 [Edge24]
  _Parent = -> Elements
FEATURE [App::FeaturePython] ElementLink070  label="_Element057"  # link proxy (typed FeaturePython)
  LinkTransform = true
  LinkedObject = -> _Element057
  _Parent = -> Constraint035
FEATURE [Part::FeaturePython] _Element057  # link proxy (typed FeaturePython)
  Detach = false
  LinkTransform = true
  LinkedObject = -> SquarePipe_SS001 [Edge13]
  _Parent = -> Elements
FEATURE [App::FeaturePython] Constraint036  label="SameOrientation016"  # WARN: FeaturePython — macro-defined, semantics opaque (R4)
  Disabled = false
  Group = -> [ElementLink071,ElementLink072]
  _ConstraintType = 2
  _Parent = -> Constraints
FEATURE [App::FeaturePython] ElementLink071  label="_Element058"  # link proxy (typed FeaturePython)
  LinkTransform = true
  LinkedObject = -> _Element058
  _Parent = -> Constraint036
FEATURE [Part::FeaturePython] _Element058  # link proxy (typed FeaturePython)
  Detach = false
  LinkTransform = true
  LinkedObject = -> Link010 [Face8]
  _Parent = -> Elements
FEATURE [App::FeaturePython] ElementLink072  label="_Element059"  # link proxy (typed FeaturePython)
  LinkTransform = true
  LinkedObject = -> _Element059
  _Parent = -> Constraint036
FEATURE [Part::FeaturePython] _Element059  # link proxy (typed FeaturePython)
  Detach = false
  LinkTransform = true
  LinkedObject = -> SquarePipe_SS001 [Face18]
  _Parent = -> Elements
FEATURE [App::FeaturePython] Constraint037  label="MidPoint017"  # WARN: FeaturePython — macro-defined, semantics opaque (R4)
  Disabled = false
  Group = -> [ElementLink073,ElementLink074]
  _ConstraintType = 20
  _Parent = -> Constraints
FEATURE [App::FeaturePython] ElementLink073  label="_Element060"  # link proxy (typed FeaturePython)
  LinkTransform = true
  LinkedObject = -> _Element060
  _Parent = -> Constraint037
FEATURE [Part::FeaturePython] _Element060  # link proxy (typed FeaturePython)
  Detach = false
  LinkTransform = true
  LinkedObject = -> Link011 [Edge24]
  _Parent = -> Elements
FEATURE [App::FeaturePython] ElementLink074  label="_Element061"  # link proxy (typed FeaturePython)
  LinkTransform = true
  LinkedObject = -> _Element061
  _Parent = -> Constraint037
FEATURE [Part::FeaturePython] _Element061  # link proxy (typed FeaturePython)
  Detach = false
  LinkTransform = true
  LinkedObject = -> SquarePipe_SS001 [Edge7]
  _Parent = -> Elements
FEATURE [App::FeaturePython] Constraint038  label="SameOrientation017"  # WARN: FeaturePython — macro-defined, semantics opaque (R4)
  Disabled = false
  Group = -> [ElementLink075,ElementLink076]
  _ConstraintType = 2
  _Parent = -> Constraints
FEATURE [App::FeaturePython] ElementLink075  label="_Element062"  # link proxy (typed FeaturePython)
  LinkTransform = true
  LinkedObject = -> _Element062
  _Parent = -> Constraint038
FEATURE [Part::FeaturePython] _Element062  # link proxy (typed FeaturePython)
  Detach = false
  LinkTransform = true
  LinkedObject = -> Link011 [Face8]
  _Parent = -> Elements
FEATURE [App::FeaturePython] ElementLink076  label="_Element059"  # link proxy (typed FeaturePython)
  LinkTransform = true
  LinkedObject = -> _Element059
  _Parent = -> Constraint038
FEATURE [App::FeaturePython] Constraint039  label="MidPoint018"  # WARN: FeaturePython — macro-defined, semantics opaque (R4)
  Disabled = false
  Group = -> [ElementLink077,ElementLink078]
  _ConstraintType = 20
  _Parent = -> Constraints
FEATURE [App::FeaturePython] ElementLink077  label="_Element063"  # link proxy (typed FeaturePython)
  LinkTransform = true
  LinkedObject = -> _Element063
  _Parent = -> Constraint039
FEATURE [Part::FeaturePython] _Element063  # link proxy (typed FeaturePython)
  Detach = false
  LinkTransform = true
  LinkedObject = -> Clone005 [Edge47]
  _Parent = -> Elements
FEATURE [App::FeaturePython] ElementLink078  label="_Element064"  # link proxy (typed FeaturePython)
  LinkTransform = true
  LinkedObject = -> _Element064
  _Parent = -> Constraint039
FEATURE [Part::FeaturePython] _Element064  # link proxy (typed FeaturePython)
  Detach = false
  LinkTransform = true
  LinkedObject = -> Link006 [Edge13]
  _Parent = -> Elements
FEATURE [App::FeaturePython] Constraint040  label="SameOrientation018"  # WARN: FeaturePython — macro-defined, semantics opaque (R4)
  Disabled = false
  Group = -> [ElementLink079,ElementLink080]
  _ConstraintType = 2
  _Parent = -> Constraints
FEATURE [App::FeaturePython] ElementLink079  label="_Element065"  # link proxy (typed FeaturePython)
  LinkTransform = true
  LinkedObject = -> _Element065
  _Parent = -> Constraint040
FEATURE [Part::FeaturePython] _Element065  # link proxy (typed FeaturePython)
  Detach = false
  LinkTransform = true
  LinkedObject = -> Clone005 [Face16]
  _Parent = -> Elements
FEATURE [App::FeaturePython] ElementLink080  label="_Element066"  # link proxy (typed FeaturePython)
  LinkTransform = true
  LinkedObject = -> _Element066
  _Parent = -> Constraint040
FEATURE [Part::FeaturePython] _Element066  # link proxy (typed FeaturePython)
  Detach = false
  LinkTransform = true
  LinkedObject = -> Link006 [Face18]
  _Parent = -> Elements
FEATURE [App::FeaturePython] Constraint041  label="MidPoint019"  # WARN: FeaturePython — macro-defined, semantics opaque (R4)
  Disabled = false
  Group = -> [ElementLink081,ElementLink082]
  _ConstraintType = 20
  _Parent = -> Constraints
FEATURE [App::FeaturePython] ElementLink081  label="_Element067"  # link proxy (typed FeaturePython)
  LinkTransform = true
  LinkedObject = -> _Element067
  _Parent = -> Constraint041
FEATURE [Part::FeaturePython] _Element067  # link proxy (typed FeaturePython)
  Detach = false
  LinkTransform = true
  LinkedObject = -> Clone006 [Edge24]
  _Parent = -> Elements
FEATURE [App::FeaturePython] ElementLink082  label="_Element068"  # link proxy (typed FeaturePython)
  LinkTransform = true
  LinkedObject = -> _Element068
  _Parent = -> Constraint041
FEATURE [Part::FeaturePython] _Element068  # link proxy (typed FeaturePython)
  Detach = false
  LinkTransform = true
  LinkedObject = -> Link006 [Edge7]
  _Parent = -> Elements
FEATURE [App::FeaturePython] Constraint042  label="SameOrientation019"  # WARN: FeaturePython — macro-defined, semantics opaque (R4)
  Disabled = false
  Group = -> [ElementLink083,ElementLink084]
  _ConstraintType = 2
  _Parent = -> Constraints
FEATURE [App::FeaturePython] ElementLink083  label="_Element069"  # link proxy (typed FeaturePython)
  LinkTransform = true
  LinkedObject = -> _Element069
  _Parent = -> Constraint042
FEATURE [Part::FeaturePython] _Element069  # link proxy (typed FeaturePython)
  Detach = false
  LinkTransform = true
  LinkedObject = -> Clone006 [Face8]
  _Parent = -> Elements
FEATURE [App::FeaturePython] ElementLink084  label="_Element066"  # link proxy (typed FeaturePython)
  LinkTransform = true
  LinkedObject = -> _Element066
  _Parent = -> Constraint042
FEATURE [App::FeaturePython] Constraint043  label="MidPoint020"  # WARN: FeaturePython — macro-defined, semantics opaque (R4)
  Disabled = false
  Group = -> [ElementLink085,ElementLink086]
  _ConstraintType = 20
  _Parent = -> Constraints
FEATURE [App::FeaturePython] ElementLink085  label="_Element070"  # link proxy (typed FeaturePython)
  LinkTransform = true
  LinkedObject = -> _Element070
  _Parent = -> Constraint043
FEATURE [Part::FeaturePython] _Element070  # link proxy (typed FeaturePython)
  Detach = false
  LinkTransform = true
  LinkedObject = -> Clone007 [Edge24]
  _Parent = -> Elements
FEATURE [App::FeaturePython] ElementLink086  label="_Element071"  # link proxy (typed FeaturePython)
  LinkTransform = true
  LinkedObject = -> _Element071
  _Parent = -> Constraint043
FEATURE [Part::FeaturePython] _Element071  # link proxy (typed FeaturePython)
  Detach = false
  LinkTransform = true
  LinkedObject = -> Link008 [Edge7]
  _Parent = -> Elements
FEATURE [App::FeaturePython] Constraint044  label="SameOrientation020"  # WARN: FeaturePython — macro-defined, semantics opaque (R4)
  Disabled = false
  Group = -> [ElementLink087,ElementLink088]
  _ConstraintType = 2
  _Parent = -> Constraints
FEATURE [App::FeaturePython] ElementLink087  label="_Element072"  # link proxy (typed FeaturePython)
  LinkTransform = true
  LinkedObject = -> _Element072
  _Parent = -> Constraint044
FEATURE [Part::FeaturePython] _Element072  # link proxy (typed FeaturePython)
  Detach = false
  LinkTransform = true
  LinkedObject = -> Clone007 [Face8]
  _Parent = -> Elements
FEATURE [App::FeaturePython] ElementLink088  label="_Element073"  # link proxy (typed FeaturePython)
  LinkTransform = true
  LinkedObject = -> _Element073
  _Parent = -> Constraint044
FEATURE [Part::FeaturePython] _Element073  # link proxy (typed FeaturePython)
  Detach = false
  LinkTransform = true
  LinkedObject = -> Link008 [Face18]
  _Parent = -> Elements
FEATURE [App::FeaturePython] Constraint045  label="MidPoint021"  # WARN: FeaturePython — macro-defined, semantics opaque (R4)
  Disabled = false
  Group = -> [ElementLink089,ElementLink090]
  _ConstraintType = 20
  _Parent = -> Constraints
FEATURE [App::FeaturePython] ElementLink089  label="_Element074"  # link proxy (typed FeaturePython)
  LinkTransform = true
  LinkedObject = -> _Element074
  _Parent = -> Constraint045
FEATURE [Part::FeaturePython] _Element074  # link proxy (typed FeaturePython)
  Detach = false
  LinkTransform = true
  LinkedObject = -> Clone008 [Edge24]
  _Parent = -> Elements
FEATURE [App::FeaturePython] ElementLink090  label="_Element075"  # link proxy (typed FeaturePython)
  LinkTransform = true
  LinkedObject = -> _Element075
  _Parent = -> Constraint045
FEATURE [Part::FeaturePython] _Element075  # link proxy (typed FeaturePython)
  Detach = false
  LinkTransform = true
  LinkedObject = -> Link005 [Edge13]
  _Parent = -> Elements
FEATURE [App::FeaturePython] Constraint046  label="SameOrientation021"  # WARN: FeaturePython — macro-defined, semantics opaque (R4)
  Disabled = false
  Group = -> [ElementLink091,ElementLink092]
  _ConstraintType = 2
  _Parent = -> Constraints
FEATURE [App::FeaturePython] ElementLink091  label="_Element076"  # link proxy (typed FeaturePython)
  LinkTransform = true
  LinkedObject = -> _Element076
  _Parent = -> Constraint046
FEATURE [Part::FeaturePython] _Element076  # link proxy (typed FeaturePython)
  Detach = false
  LinkTransform = true
  LinkedObject = -> Clone008 [Face8]
  _Parent = -> Elements
FEATURE [App::FeaturePython] ElementLink092  label="_Element077"  # link proxy (typed FeaturePython)
  LinkTransform = true
  LinkedObject = -> _Element077
  _Parent = -> Constraint046
FEATURE [Part::FeaturePython] _Element077  # link proxy (typed FeaturePython)
  Detach = false
  LinkTransform = true
  LinkedObject = -> Link005 [Face18]
  _Parent = -> Elements
FEATURE [App::FeaturePython] Constraint047  label="MidPoint022"  # WARN: FeaturePython — macro-defined, semantics opaque (R4)
  Disabled = false
  Group = -> [ElementLink093,ElementLink094]
  _ConstraintType = 20
  _Parent = -> Constraints
FEATURE [App::FeaturePython] ElementLink093  label="_Element078"  # link proxy (typed FeaturePython)
  LinkTransform = true
  LinkedObject = -> _Element078
  _Parent = -> Constraint047
FEATURE [Part::FeaturePython] _Element078  # link proxy (typed FeaturePython)
  Detach = false
  LinkTransform = true
  LinkedObject = -> Clone009 [Edge47]
  _Parent = -> Elements
FEATURE [App::FeaturePython] ElementLink094  label="_Element079"  # link proxy (typed FeaturePython)
  LinkTransform = true
  LinkedObject = -> _Element079
  _Parent = -> Constraint047
FEATURE [Part::FeaturePython] _Element079  # link proxy (typed FeaturePython)
  Detach = false
  LinkTransform = true
  LinkedObject = -> Link007 [Edge13]
  _Parent = -> Elements
FEATURE [App::FeaturePython] Constraint048  label="SameOrientation022"  # WARN: FeaturePython — macro-defined, semantics opaque (R4)
  Disabled = false
  Group = -> [ElementLink095,ElementLink096]
  _ConstraintType = 2
  _Parent = -> Constraints
FEATURE [App::FeaturePython] ElementLink095  label="_Element080"  # link proxy (typed FeaturePython)
  LinkTransform = true
  LinkedObject = -> _Element080
  _Parent = -> Constraint048
FEATURE [Part::FeaturePython] _Element080  # link proxy (typed FeaturePython)
  Detach = false
  LinkTransform = true
  LinkedObject = -> Clone009 [Face16]
  _Parent = -> Elements
FEATURE [App::FeaturePython] ElementLink096  label="_Element081"  # link proxy (typed FeaturePython)
  LinkTransform = true
  LinkedObject = -> _Element081
  _Parent = -> Constraint048
FEATURE [Part::FeaturePython] _Element081  # link proxy (typed FeaturePython)
  Detach = false
  LinkTransform = true
  LinkedObject = -> Link007 [Face18]
  _Parent = -> Elements
FEATURE [App::FeaturePython] Constraint049  label="MidPoint023"  # WARN: FeaturePython — macro-defined, semantics opaque (R4)
  Disabled = false
  Group = -> [ElementLink097,ElementLink098]
  _ConstraintType = 20
  _Parent = -> Constraints
FEATURE [App::FeaturePython] ElementLink097  label="_Element082"  # link proxy (typed FeaturePython)
  LinkTransform = true
  LinkedObject = -> _Element082
  _Parent = -> Constraint049
FEATURE [Part::FeaturePython] _Element082  # link proxy (typed FeaturePython)
  Detach = false
  LinkTransform = true
  LinkedObject = -> Link003 [Edge47]
  _Parent = -> Elements
FEATURE [App::FeaturePython] ElementLink098  label="_Element037"  # link proxy (typed FeaturePython)
  LinkTransform = true
  LinkedObject = -> _Element037
  _Parent = -> Constraint049
FEATURE [App::FeaturePython] Constraint050  label="SameOrientation023"  # WARN: FeaturePython — macro-defined, semantics opaque (R4)
  Disabled = false
  Group = -> [ElementLink099,ElementLink100]
  _ConstraintType = 2
  _Parent = -> Constraints
FEATURE [App::FeaturePython] ElementLink099  label="_Element083"  # link proxy (typed FeaturePython)
  LinkTransform = true
  LinkedObject = -> _Element083
  _Parent = -> Constraint050
FEATURE [Part::FeaturePython] _Element083  # link proxy (typed FeaturePython)
  Detach = false
  LinkTransform = true
  LinkedObject = -> Link003 [Face16]
  _Parent = -> Elements
FEATURE [App::FeaturePython] ElementLink100  label="_Element035"  # link proxy (typed FeaturePython)
  LinkTransform = true
  LinkedObject = -> _Element035
  _Parent = -> Constraint050
FEATURE [App::FeaturePython] Constraint051  label="MidPoint024"  # WARN: FeaturePython — macro-defined, semantics opaque (R4)
  Disabled = false
  Group = -> [ElementLink101,ElementLink102]
  _ConstraintType = 20
  _Parent = -> Constraints
FEATURE [App::FeaturePython] ElementLink101  label="_Element084"  # link proxy (typed FeaturePython)
  LinkTransform = true
  LinkedObject = -> _Element084
  _Parent = -> Constraint051
FEATURE [Part::FeaturePython] _Element084  # link proxy (typed FeaturePython)
  Detach = false
  LinkTransform = true
  LinkedObject = -> H200x100x5_5_011 [Edge47]
  _Parent = -> Elements
FEATURE [App::FeaturePython] ElementLink102  label="_Element085"  # link proxy (typed FeaturePython)
  LinkTransform = true
  LinkedObject = -> _Element085
  _Parent = -> Constraint051
FEATURE [Part::FeaturePython] _Element085  # link proxy (typed FeaturePython)
  Detach = false
  LinkTransform = true
  LinkedObject = -> Link003 [Edge1]
  _Parent = -> Elements
FEATURE [App::FeaturePython] Constraint052  label="SameOrientation024"  # WARN: FeaturePython — macro-defined, semantics opaque (R4)
  Disabled = false
  Group = -> [ElementLink103,ElementLink104]
  _ConstraintType = 2
  _Parent = -> Constraints
FEATURE [App::FeaturePython] ElementLink103  label="_Element086"  # link proxy (typed FeaturePython)
  LinkTransform = true
  LinkedObject = -> _Element086
  _Parent = -> Constraint052
FEATURE [Part::FeaturePython] _Element086  # link proxy (typed FeaturePython)
  Detach = false
  LinkTransform = true
  LinkedObject = -> H200x100x5_5_011 [Face16]
  _Parent = -> Elements
FEATURE [App::FeaturePython] ElementLink104  label="_Element083"  # link proxy (typed FeaturePython)
  LinkTransform = true
  LinkedObject = -> _Element083
  _Parent = -> Constraint052
FEATURE [App::FeaturePython] Constraint053  label="MidPoint025"  # WARN: FeaturePython — macro-defined, semantics opaque (R4)
  Disabled = false
  Group = -> [ElementLink105,ElementLink106]
  _ConstraintType = 20
  _Parent = -> Constraints
FEATURE [App::FeaturePython] ElementLink105  label="_Element087"  # link proxy (typed FeaturePython)
  LinkTransform = true
  LinkedObject = -> _Element087
  _Parent = -> Constraint053
FEATURE [Part::FeaturePython] _Element087  # link proxy (typed FeaturePython)
  Detach = false
  LinkTransform = true
  LinkedObject = -> Clone004 [Edge47]
  _Parent = -> Elements
FEATURE [App::FeaturePython] ElementLink106  label="_Element088"  # link proxy (typed FeaturePython)
  LinkTransform = true
  LinkedObject = -> _Element088
  _Parent = -> Constraint053
FEATURE [Part::FeaturePython] _Element088  # link proxy (typed FeaturePython)
  Detach = false
  LinkTransform = true
  LinkedObject = -> Clone001 [Edge1]
  _Parent = -> Elements
FEATURE [App::FeaturePython] Constraint054  label="SameOrientation025"  # WARN: FeaturePython — macro-defined, semantics opaque (R4)
  Disabled = false
  Group = -> [ElementLink107,ElementLink108]
  _ConstraintType = 2
  _Parent = -> Constraints
FEATURE [App::FeaturePython] ElementLink107  label="_Element089"  # link proxy (typed FeaturePython)
  LinkTransform = true
  LinkedObject = -> _Element089
  _Parent = -> Constraint054
FEATURE [Part::FeaturePython] _Element089  # link proxy (typed FeaturePython)
  Detach = false
  LinkTransform = true
  LinkedObject = -> Clone004 [Face16]
  _Parent = -> Elements
FEATURE [App::FeaturePython] ElementLink108  label="_Element048"  # link proxy (typed FeaturePython)
  LinkTransform = true
  LinkedObject = -> _Element048
  _Parent = -> Constraint054
FEATURE [Part::FeaturePython] _Element090  # link proxy (typed FeaturePython)
  Detach = false
  LinkTransform = true
  LinkedObject = -> C150x75x007 [Edge35]
  _Parent = -> Elements
FEATURE [Part::FeaturePython] _Element091  # link proxy (typed FeaturePython)
  Detach = false
  LinkTransform = true
  LinkedObject = -> Clone [Edge44]
  _Parent = -> Elements
FEATURE [App::FeaturePython] Constraint055  label="PointDistance"  # WARN: FeaturePython — macro-defined, semantics opaque (R4)
  Disabled = false
  Distance = 1000
  Group = -> [ElementLink109,ElementLink110]
  _ConstraintType = 5
  _Parent = -> Constraints
FEATURE [App::FeaturePython] ElementLink109  label="_Element092"  # link proxy (typed FeaturePython)
  LinkTransform = true
  LinkedObject = -> _Element092
  _Parent = -> Constraint055
FEATURE [Part::FeaturePython] _Element092  # link proxy (typed FeaturePython)
  Detach = false
  LinkTransform = true
  LinkedObject = -> C150x75x007 [Vertex2]
  _Parent = -> Elements
FEATURE [App::FeaturePython] ElementLink110  label="_Element093"  # link proxy (typed FeaturePython)
  LinkTransform = true
  LinkedObject = -> _Element093
  _Parent = -> Constraint055
FEATURE [Part::FeaturePython] _Element093  # link proxy (typed FeaturePython)
  Detach = false
  LinkTransform = true
  LinkedObject = -> H200x100x5_5_010 [Edge44]
  _Parent = -> Elements
FEATURE [App::FeaturePython] Constraint056  label="SameOrientation026"  # WARN: FeaturePython — macro-defined, semantics opaque (R4)
  Disabled = false
  Group = -> [ElementLink111,ElementLink112]
  _ConstraintType = 2
  _Parent = -> Constraints
FEATURE [App::FeaturePython] ElementLink111  label="_Element094"  # link proxy (typed FeaturePython)
  LinkTransform = true
  LinkedObject = -> _Element094
  _Parent = -> Constraint056
FEATURE [Part::FeaturePython] _Element094  # link proxy (typed FeaturePython)
  Detach = false
  LinkTransform = true
  LinkedObject = -> C150x75x007 [Face12]
  _Parent = -> Elements
FEATURE [App::FeaturePython] ElementLink112  label="_Element029"  # link proxy (typed FeaturePython)
  LinkTransform = true
  LinkedObject = -> _Element029
  _Parent = -> Constraint056
FEATURE [App::FeaturePython] Constraint057  label="AxialAlignment"  # WARN: FeaturePython — macro-defined, semantics opaque (R4)
  Angle = 0
  AnglePitch = 0
  AngleRoll = 0
  Disabled = false
  Group = -> [ElementLink113,ElementLink114]
  LockAngle = false
  Multiply = false
  _ConstraintType = 36
  _Parent = -> Constraints
FEATURE [App::FeaturePython] ElementLink113  label="_Element090"  # link proxy (typed FeaturePython)
  LinkTransform = true
  LinkedObject = -> _Element090
  _Parent = -> Constraint057
FEATURE [App::FeaturePython] ElementLink114  label="_Element091"  # link proxy (typed FeaturePython)
  LinkTransform = true
  LinkedObject = -> _Element091
  _Parent = -> Constraint057
FEATURE [App::FeaturePython] Constraint058  label="AxialAlignment001"  # WARN: FeaturePython — macro-defined, semantics opaque (R4)
  Angle = 0
  AnglePitch = 0
  AngleRoll = 0
  Disabled = false
  Group = -> [ElementLink115,ElementLink116]
  LockAngle = false
  Multiply = false
  _ConstraintType = 36
  _Parent = -> Constraints
FEATURE [App::FeaturePython] ElementLink115  label="_Element095"  # link proxy (typed FeaturePython)
  LinkTransform = true
  LinkedObject = -> _Element095
  _Parent = -> Constraint058
FEATURE [Part::FeaturePython] _Element095  # link proxy (typed FeaturePython)
  Detach = false
  LinkTransform = true
  LinkedObject = -> C150x75x008 [Edge1]
  _Parent = -> Elements
FEATURE [App::FeaturePython] ElementLink116  label="_Element096"  # link proxy (typed FeaturePython)
  LinkTransform = true
  LinkedObject = -> _Element096
  _Parent = -> Constraint058
FEATURE [Part::FeaturePython] _Element096  # link proxy (typed FeaturePython)
  Detach = false
  LinkTransform = true
  LinkedObject = -> C150x75x007 [Edge1]
  _Parent = -> Elements
FEATURE [App::FeaturePython] Constraint059  label="SameOrientation027"  # WARN: FeaturePython — macro-defined, semantics opaque (R4)
  Disabled = false
  Group = -> [ElementLink117,ElementLink118]
  _ConstraintType = 2
  _Parent = -> Constraints
FEATURE [App::FeaturePython] ElementLink117  label="_Element097"  # link proxy (typed FeaturePython)
  LinkTransform = true
  LinkedObject = -> _Element097
  _Parent = -> Constraint059
FEATURE [Part::FeaturePython] _Element097  # link proxy (typed FeaturePython)
  Detach = false
  LinkTransform = true
  LinkedObject = -> C150x75x008 [Face12]
  _Parent = -> Elements
FEATURE [App::FeaturePython] ElementLink118  label="_Element026"  # link proxy (typed FeaturePython)
  LinkTransform = true
  LinkedObject = -> _Element026
  _Parent = -> Constraint059
